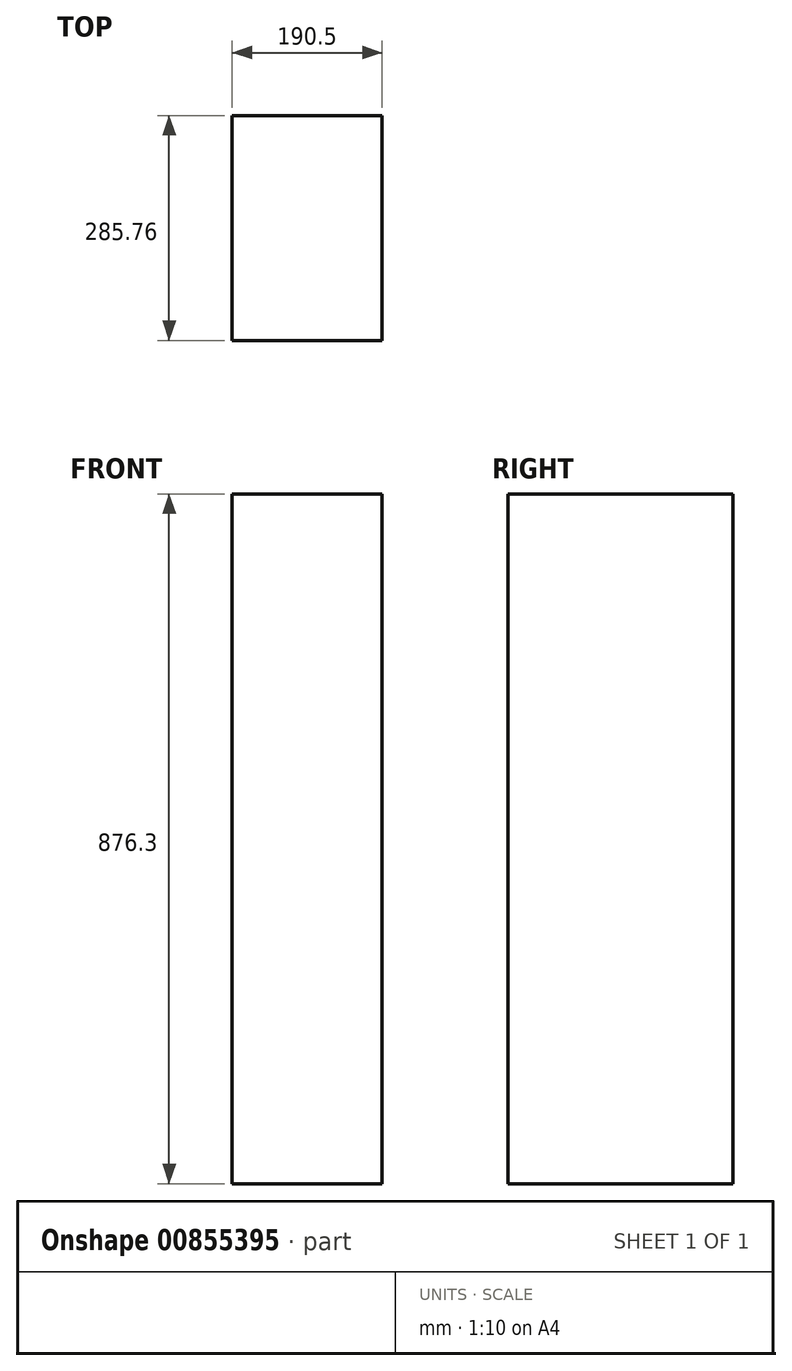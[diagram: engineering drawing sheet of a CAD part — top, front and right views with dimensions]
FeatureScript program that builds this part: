
annotation { "Feature Type Name" : "Feature", "Feature Type Description" : "" }
export const myFeature = defineFeature(function(context is Context, id is Id, definition is map)
    precondition{}
    {
        {
            var Q0;
            Q0=qCreatedBy(makeId("Top.planeOp"),FACE);
            var sketch = newSketch(context, id + "F0", { "sketchPlane" : qUnion([Q0])});
            skLineSegment(sketch, "E0.bottom", {"start": v(-95.25, -142.88) * mm, "end": v(95.25, -142.88) * mm});
            skLineSegment(sketch, "E0.top", {"start": v(-95.25, 142.88) * mm, "end": v(95.25, 142.88) * mm});
            skLineSegment(sketch, "E0.left", {"start": v(-95.25, -142.88) * mm, "end": v(-95.25, 142.88) * mm});
            skLineSegment(sketch, "E0.right", {"start": v(95.25, -142.88) * mm, "end": v(95.25, 142.87) * mm});
            skPoint(sketch, "E0.middle", {"position": v(0, 0) * mm});
            skSolve(sketch);
        }
        {
            var Q0;
            Q0=makeQuery(id+"F0.imprint","IMPRINT",FACE,{"disambiguationData":[TD([[makeQuery(id+"F0.imprint","IMPRINT",EDGE,{"derivedFrom":sQuery(id+"F0.wireOp",EDGE,"E0.bottom")}),1.0]])]});
            extrude(context, id + "F1", {"entities" : qUnion([Q0]), "oppositeDirection" : true, "depth" : 876.3 * mm, "offsetDistance" : 25 * mm});
        }
    });
